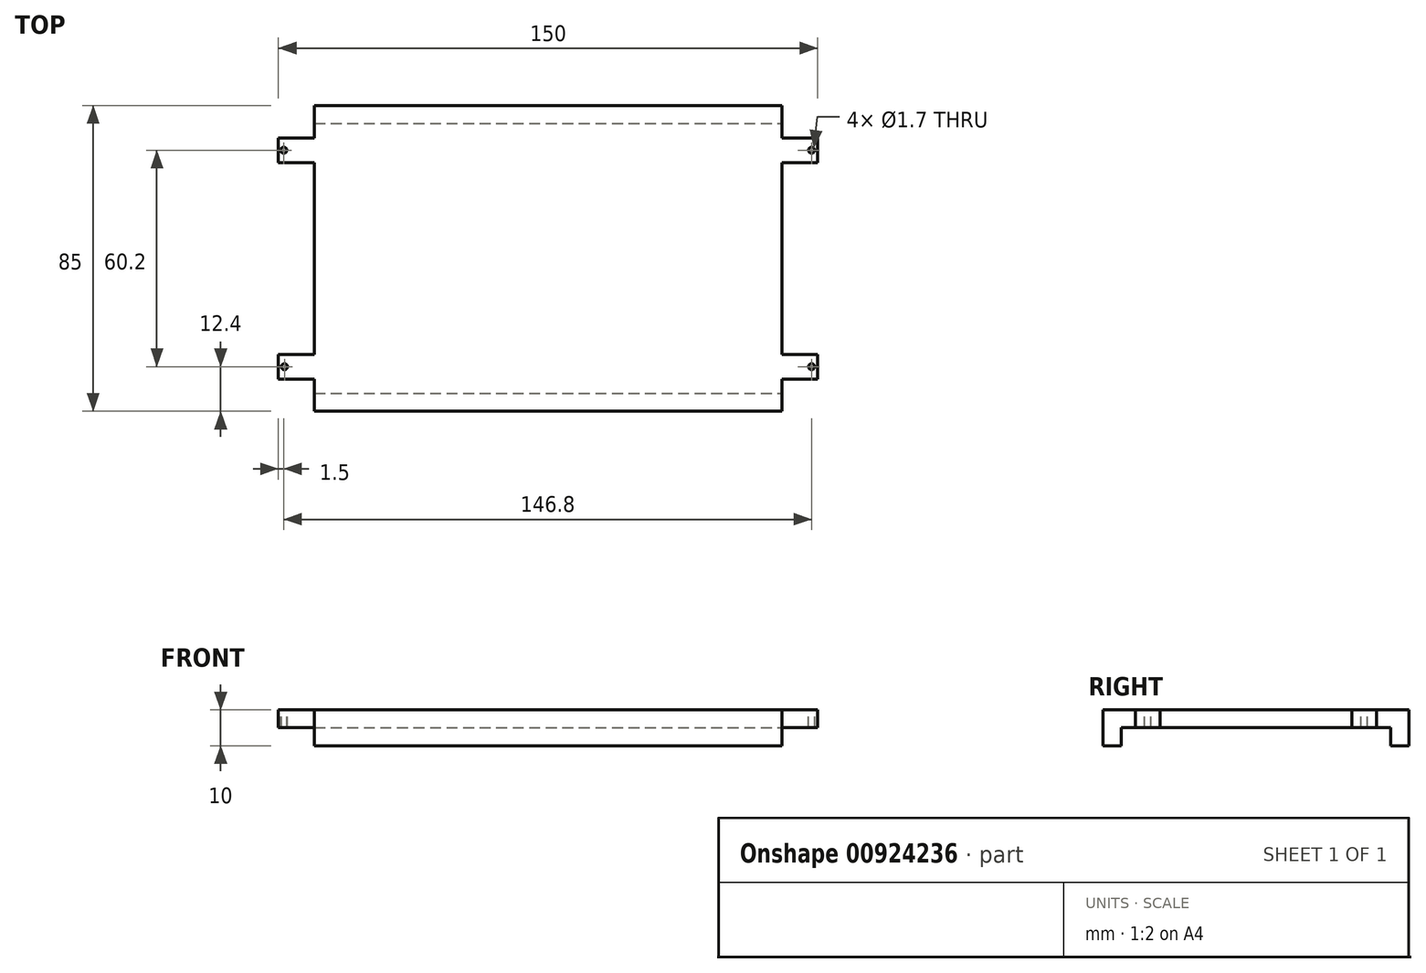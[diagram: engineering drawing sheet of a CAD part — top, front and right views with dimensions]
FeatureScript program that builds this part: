
annotation { "Feature Type Name" : "Feature", "Feature Type Description" : "" }
export const myFeature = defineFeature(function(context is Context, id is Id, definition is map)
    precondition{}
    {
        {
            var Q0;
            Q0=qCreatedBy(makeId("Top.planeOp"),FACE);
            var sketch = newSketch(context, id + "F0", { "sketchPlane" : qUnion([Q0])});
            skLineSegment(sketch, "E0.bottom", {"start": v(75, -33.5) * mm, "end": v(-75, -33.5) * mm});
            skLineSegment(sketch, "E0.top", {"start": v(75, 33.5) * mm, "end": v(-75, 33.5) * mm});
            skLineSegment(sketch, "E0.left", {"start": v(75, -33.5) * mm, "end": v(75, 33.5) * mm});
            skLineSegment(sketch, "E0.right", {"start": v(-75, -33.5) * mm, "end": v(-75, 33.5) * mm});
            skPoint(sketch, "E0.middle", {"position": v(0, 0) * mm});
            skPoint(sketch, "E1", {"position": v(-65, 26.7) * mm});
            skPoint(sketch, "E2", {"position": v(-65, -26.7) * mm});
            skPoint(sketch, "E3", {"position": v(65, -26.7) * mm});
            skPoint(sketch, "E4", {"position": v(65, 26.7) * mm});
            skLineSegment(sketch, "E5", {"start": v(-75, 26.7) * mm, "end": v(-65, 26.7) * mm});
            skLineSegment(sketch, "E6", {"start": v(-65, -26.7) * mm, "end": v(-75, -26.7) * mm});
            skLineSegment(sketch, "E7", {"start": v(-75, -26.7) * mm, "end": v(-65, -26.7) * mm});
            skLineSegment(sketch, "E8", {"start": v(-65, 26.7) * mm, "end": v(-65, -26.7) * mm});
            skLineSegment(sketch, "E9", {"start": v(65, 26.7) * mm, "end": v(65, -26.7) * mm});
            skLineSegment(sketch, "E10", {"start": v(65, -26.7) * mm, "end": v(75, -26.7) * mm});
            skLineSegment(sketch, "E11", {"start": v(65, 26.7) * mm, "end": v(75, 26.7) * mm});
            skSolve(sketch);
        }
        {
            var Q0;
            {var subQ4=sQuery(id+"F0.wireOp",EDGE,"E0.bottom");Q0=makeQuery(id+"F0.imprint","IMPRINT",FACE,{"disambiguationData":[TD([[makeQuery(id+"F0.imprint","IMPRINT",EDGE,{"derivedFrom":subQ4}),-1.0]])]});}
            extrude(context, id + "F1", {"entities" : qUnion([Q0]), "depth" : 4.9 * mm, "offsetDistance" : 25 * mm});
        }
        {
            var Q0;
            Q0=makeQuery(id+"F1.opExtrude","CAP_FACE",FACE,{"disambiguationData":[OSD([sQuery(id+"F0.wireOp",EDGE,"E0.bottom"),sQuery(id+"F0.wireOp",EDGE,"E0.top"),sQuery(id+"F0.wireOp",EDGE,"E0.left"),sQuery(id+"F0.wireOp",EDGE,"E0.right"),sQuery(id+"F0.wireOp",EDGE,"E5"),sQuery(id+"F0.wireOp",EDGE,"E7"),sQuery(id+"F0.wireOp",EDGE,"E8"),sQuery(id+"F0.wireOp",EDGE,"E9"),sQuery(id+"F0.wireOp",EDGE,"E10"),sQuery(id+"F0.wireOp",EDGE,"E11")])],"isStart":false});
            var sketch = newSketch(context, id + "F2", { "sketchPlane" : qUnion([Q0])});
            skPoint(sketch, "E12", {"position": v(-73.5, 30.1) * mm});
            skPoint(sketch, "E13", {"position": v(-73.3, -30.1) * mm});
            skPoint(sketch, "E14", {"position": v(73.3, 30.1) * mm});
            skPoint(sketch, "E15", {"position": v(73.3, -30.1) * mm});
            skCircle(sketch, "E16", {"center": v(-73.5, 30.1) * mm, "radius": 0.85 * mm});
            skCircle(sketch, "E17", {"center": v(-73.3, -30.1) * mm, "radius": 0.85 * mm});
            skCircle(sketch, "E18", {"center": v(73.3, 30.1) * mm, "radius": 0.85 * mm});
            skCircle(sketch, "E19", {"center": v(73.3, -30.1) * mm, "radius": 0.85 * mm});
            skSolve(sketch);
        }
        {
            var Q0;
            Q0=makeQuery(id+"F2.imprint","IMPRINT",FACE,{"disambiguationData":[TD([[makeQuery(id+"F2.imprint","IMPRINT",EDGE,{"derivedFrom":sQuery(id+"F2.wireOp",EDGE,"E16")}),1.0]])]});
            var Q1;
            Q1=makeQuery(id+"F2.imprint","IMPRINT",FACE,{"disambiguationData":[TD([[makeQuery(id+"F2.imprint","IMPRINT",EDGE,{"derivedFrom":sQuery(id+"F2.wireOp",EDGE,"E17")}),1.0]])]});
            var Q2;
            Q2=makeQuery(id+"F2.imprint","IMPRINT",FACE,{"disambiguationData":[TD([[makeQuery(id+"F2.imprint","IMPRINT",EDGE,{"derivedFrom":sQuery(id+"F2.wireOp",EDGE,"E18")}),1.0]])]});
            var Q3;
            Q3=makeQuery(id+"F2.imprint","IMPRINT",FACE,{"disambiguationData":[TD([[makeQuery(id+"F2.imprint","IMPRINT",EDGE,{"derivedFrom":sQuery(id+"F2.wireOp",EDGE,"E19")}),1.0]])]});
            extrude(context, id + "F3", {"entities" : qUnion([Q0, Q1, Q2, Q3]), "operationType" : NewBodyOperationType.REMOVE, "endBound" : BoundingType.THROUGH_ALL, "oppositeDirection" : true, "depth" : 25 * mm, "offsetDistance" : 25 * mm});
        }
        {
            var Q0;
            Q0=makeQuery(id+"F1.opExtrude","CAP_FACE",FACE,{"disambiguationData":[OSD([sQuery(id+"F0.wireOp",EDGE,"E0.bottom"),sQuery(id+"F0.wireOp",EDGE,"E0.top"),sQuery(id+"F0.wireOp",EDGE,"E0.left"),sQuery(id+"F0.wireOp",EDGE,"E0.right"),sQuery(id+"F0.wireOp",EDGE,"E5"),sQuery(id+"F0.wireOp",EDGE,"E7"),sQuery(id+"F0.wireOp",EDGE,"E8"),sQuery(id+"F0.wireOp",EDGE,"E9"),sQuery(id+"F0.wireOp",EDGE,"E10"),sQuery(id+"F0.wireOp",EDGE,"E11")])],"isStart":false});
            var sketch = newSketch(context, id + "F4", { "sketchPlane" : qUnion([Q0])});
            skLineSegment(sketch, "E20.bottom", {"start": v(-65, 33.5) * mm, "end": v(65, 33.5) * mm});
            skLineSegment(sketch, "E20.top", {"start": v(-65, 42.5) * mm, "end": v(65, 42.5) * mm});
            skLineSegment(sketch, "E20.left", {"start": v(-65, 33.5) * mm, "end": v(-65, 42.5) * mm});
            skLineSegment(sketch, "E20.right", {"start": v(65, 33.5) * mm, "end": v(65, 42.5) * mm});
            skLineSegment(sketch, "E21", {"start": v(0, 33.5) * mm, "end": v(0, -33.5) * mm, "construction": true});
            skLineSegment(sketch, "E22.bottom", {"start": v(-65, -33.5) * mm, "end": v(65, -33.5) * mm});
            skLineSegment(sketch, "E22.top", {"start": v(-65, -42.5) * mm, "end": v(65, -42.5) * mm});
            skLineSegment(sketch, "E22.left", {"start": v(-65, -33.5) * mm, "end": v(-65, -42.5) * mm});
            skLineSegment(sketch, "E22.right", {"start": v(65, -33.5) * mm, "end": v(65, -42.5) * mm});
            skLineSegment(sketch, "E23", {"start": v(-65, 37.5) * mm, "end": v(65, 37.5) * mm});
            skPoint(sketch, "E23.endSnap0", {"position": v(65, 38) * mm});
            skLineSegment(sketch, "E24", {"start": v(-65, -37.5) * mm, "end": v(65, -37.5) * mm});
            skSolve(sketch);
        }
        {
            var Q0;
            {var subQ0=sQuery(id+"F4.wireOp",EDGE,"E20.bottom");Q0=makeQuery(id+"F4.imprint","IMPRINT",FACE,{"disambiguationData":[TD([[makeQuery(id+"F4.imprint","IMPRINT",EDGE,{"derivedFrom":subQ0}),-1.0]])]});}
            var Q1;
            {var subQ0=sQuery(id+"F4.wireOp",EDGE,"E22.bottom");Q1=makeQuery(id+"F4.imprint","IMPRINT",FACE,{"disambiguationData":[TD([[makeQuery(id+"F4.imprint","IMPRINT",EDGE,{"derivedFrom":subQ0}),1.0]])]});}
            extrude(context, id + "F5", {"entities" : qUnion([Q0, Q1]), "operationType" : NewBodyOperationType.ADD, "oppositeDirection" : true, "depth" : 4.9 * mm, "offsetDistance" : 25 * mm});
        }
        {
            var Q0;
            Q0=makeQuery(id+"F5.boolean.opBoolean","MERGE",FACE,{"derivedFrom":[makeQuery(id+"F1.opExtrude","CAP_FACE",FACE,{"disambiguationData":[OSD([sQuery(id+"F0.wireOp",EDGE,"E0.bottom"),sQuery(id+"F0.wireOp",EDGE,"E0.top"),sQuery(id+"F0.wireOp",EDGE,"E0.left"),sQuery(id+"F0.wireOp",EDGE,"E0.right"),sQuery(id+"F0.wireOp",EDGE,"E5"),sQuery(id+"F0.wireOp",EDGE,"E7"),sQuery(id+"F0.wireOp",EDGE,"E8"),sQuery(id+"F0.wireOp",EDGE,"E9"),sQuery(id+"F0.wireOp",EDGE,"E10"),sQuery(id+"F0.wireOp",EDGE,"E11")])],"isStart":false}),makeQuery(id+"F5.opExtrude","CAP_FACE",FACE,{"disambiguationData":[OSD([sQuery(id+"F4.wireOp",EDGE,"E20.bottom"),sQuery(id+"F4.wireOp",EDGE,"E20.left"),sQuery(id+"F4.wireOp",EDGE,"E20.right"),sQuery(id+"F4.wireOp",EDGE,"E23")])],"isStart":true}),makeQuery(id+"F5.opExtrude","CAP_FACE",FACE,{"disambiguationData":[OSD([sQuery(id+"F4.wireOp",EDGE,"E22.bottom"),sQuery(id+"F4.wireOp",EDGE,"E22.left"),sQuery(id+"F4.wireOp",EDGE,"E22.right"),sQuery(id+"F4.wireOp",EDGE,"E24")])],"isStart":true})]});
            var sketch = newSketch(context, id + "F6", { "sketchPlane" : qUnion([Q0])});
            skLineSegment(sketch, "E25.bottom", {"start": v(-65, 37.5) * mm, "end": v(65, 37.5) * mm});
            skLineSegment(sketch, "E25.top", {"start": v(-65, 42.5) * mm, "end": v(65, 42.5) * mm});
            skLineSegment(sketch, "E25.left", {"start": v(-65, 37.5) * mm, "end": v(-65, 42.5) * mm});
            skLineSegment(sketch, "E25.right", {"start": v(65, 37.5) * mm, "end": v(65, 42.5) * mm});
            skLineSegment(sketch, "E26.bottom", {"start": v(-65, -37.5) * mm, "end": v(65, -37.5) * mm});
            skLineSegment(sketch, "E26.top", {"start": v(-65, -42.5) * mm, "end": v(65, -42.5) * mm});
            skLineSegment(sketch, "E26.left", {"start": v(-65, -37.5) * mm, "end": v(-65, -42.5) * mm});
            skLineSegment(sketch, "E26.right", {"start": v(65, -37.5) * mm, "end": v(65, -42.5) * mm});
            skSolve(sketch);
        }
        {
            var Q0;
            Q0 = qSketchRegion(id + "F6", true);
            extrude(context, id + "F7", {"entities" : qUnion([Q0]), "operationType" : NewBodyOperationType.ADD, "oppositeDirection" : true, "depth" : 10 * mm, "offsetDistance" : 25 * mm});
        }
    });
